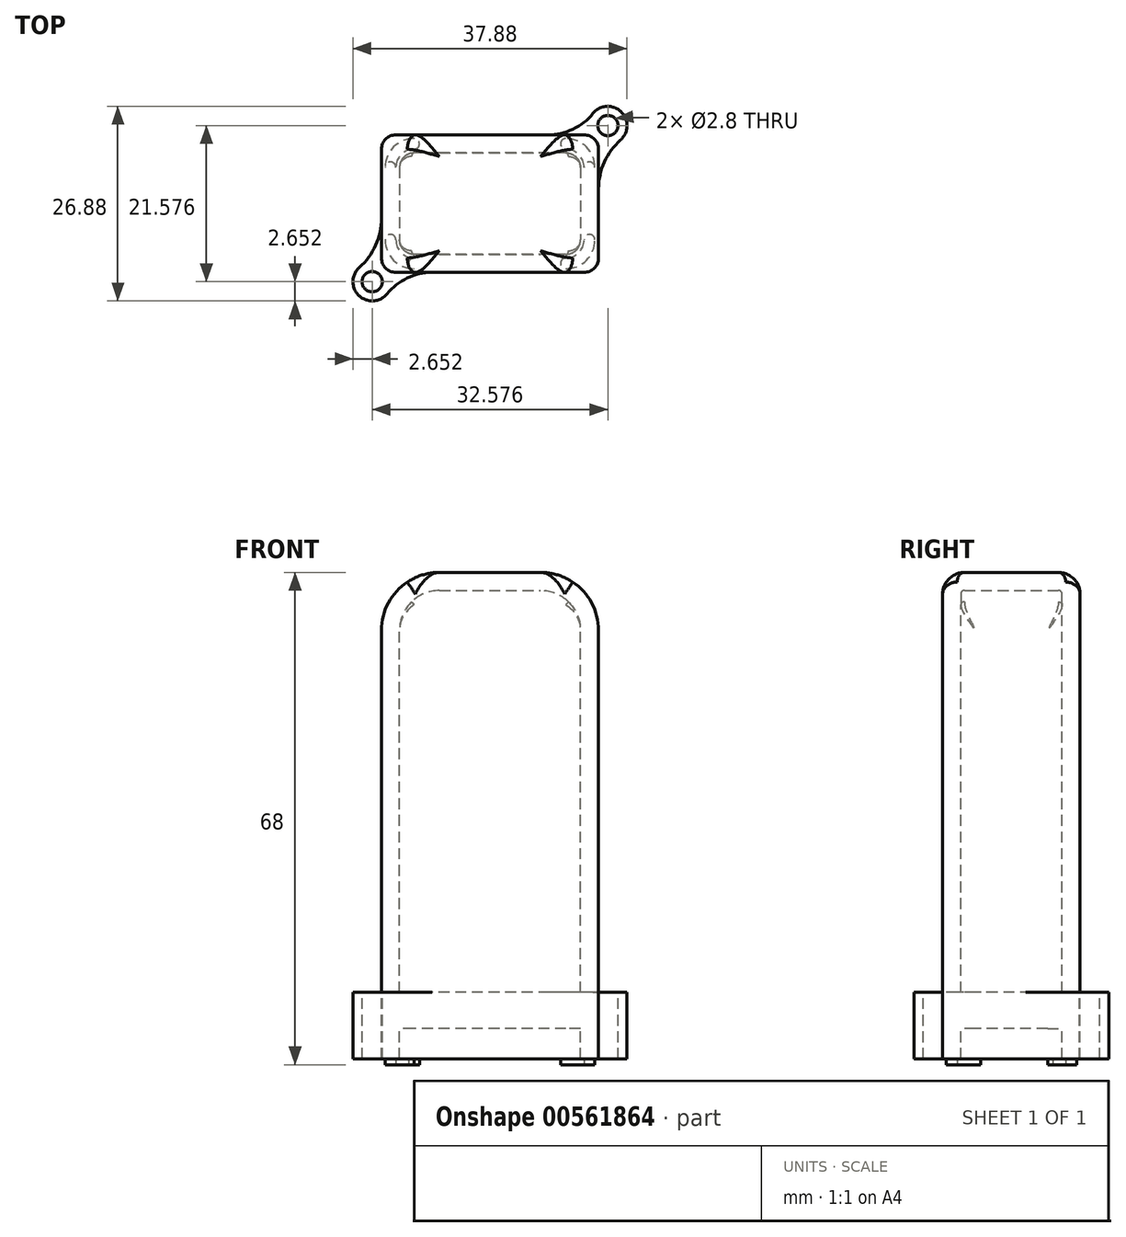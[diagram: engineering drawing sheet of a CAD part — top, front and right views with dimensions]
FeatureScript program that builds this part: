
annotation { "Feature Type Name" : "Feature", "Feature Type Description" : "" }
export const myFeature = defineFeature(function(context is Context, id is Id, definition is map)
    precondition{}
    {
        {
            var Q0;
            Q0=qCreatedBy(makeId("Top.planeOp"),FACE);
            var sketch = newSketch(context, id + "F0", { "sketchPlane" : qUnion([Q0])});
            skLineSegment(sketch, "E0.bottom", {"start": v(15, 9.5) * mm, "end": v(-15, 9.5) * mm});
            skLineSegment(sketch, "E0.top", {"start": v(15, -9.5) * mm, "end": v(-15, -9.5) * mm});
            skLineSegment(sketch, "E0.left", {"start": v(15, 9.5) * mm, "end": v(15, -9.5) * mm});
            skLineSegment(sketch, "E0.right", {"start": v(-15, 9.5) * mm, "end": v(-15, -9.5) * mm});
            skPoint(sketch, "E0.middle", {"position": v(0, 0) * mm});
            skSolve(sketch);
        }
        {
            var Q0;
            Q0 = qSketchRegion(id + "F0", true);
            extrude(context, id + "F1", {"entities" : qUnion([Q0]), "depth" : 58 * mm, "offsetDistance" : 25 * mm});
        }
        {
            var Q0;
            Q0=makeQuery(id+"F1.opExtrude","SWEPT_EDGE",EDGE,{"disambiguationData":[OSD([sQuery(id+"F0.wireOp",EDGE,"E0.top"),sQuery(id+"F0.wireOp",EDGE,"E0.right")])]});
            var Q1;
            Q1=makeQuery(id+"F1.opExtrude","SWEPT_EDGE",EDGE,{"disambiguationData":[OSD([sQuery(id+"F0.wireOp",EDGE,"E0.top"),sQuery(id+"F0.wireOp",EDGE,"E0.left")])]});
            var Q2;
            Q2=makeQuery(id+"F1.opExtrude","SWEPT_EDGE",EDGE,{"disambiguationData":[OSD([sQuery(id+"F0.wireOp",EDGE,"E0.bottom"),sQuery(id+"F0.wireOp",EDGE,"E0.left")])]});
            var Q3;
            Q3=makeQuery(id+"F1.opExtrude","SWEPT_EDGE",EDGE,{"disambiguationData":[OSD([sQuery(id+"F0.wireOp",EDGE,"E0.bottom"),sQuery(id+"F0.wireOp",EDGE,"E0.right")])]});
            fillet(context, id + "F2", {"entities" : qUnion([Q0, Q1, Q2, Q3]), "radius" : 2 * mm, "tangentPropagation" : true, "allowEdgeOverflow" : false});
        }
        {
            var Q0;
            Q0=makeQuery(id+"F1.opExtrude","CAP_EDGE",EDGE,{"disambiguationData":[OSD([sQuery(id+"F0.wireOp",EDGE,"E0.right")])],"isStart":false});
            var Q1;
            Q1=makeQuery(id+"F1.opExtrude","CAP_EDGE",EDGE,{"disambiguationData":[OSD([sQuery(id+"F0.wireOp",EDGE,"E0.left")])],"isStart":false});
            fillet(context, id + "F3", {"entities" : qUnion([Q0, Q1]), "radius" : 8 * mm, "allowEdgeOverflow" : false});
        }
        {
            var Q0;
            {var subQ0=sQuery(id+"F0.wireOp",EDGE,"E0.right");Q0=makeQuery(id+"F3.opFillet","BLEND_EDGE",EDGE,{"blendedFrom":[makeQuery(id+"F1.opExtrude","CAP_EDGE",EDGE,{"disambiguationData":[OSD([subQ0])],"isStart":false}),makeQuery(id+"F2.opFillet","BLEND_FACE",FACE,{"disambiguationData":[OSD([sQuery(id+"F0.wireOp",EDGE,"E0.top"),subQ0])]})],"blendedInto":[makeQuery(id+"F2.opFillet","BLEND_FACE",FACE,{"disambiguationData":[OSD([sQuery(id+"F0.wireOp",EDGE,"E0.top"),subQ0])]})]});}
            var Q1;
            Q1=makeQuery(id+"F3.opFillet","BLEND_EDGE",EDGE,{"blendedFrom":[makeQuery(id+"F1.opExtrude","CAP_EDGE",EDGE,{"disambiguationData":[OSD([sQuery(id+"F0.wireOp",EDGE,"E0.right")])],"isStart":false}),makeQuery(id+"F1.opExtrude","SWEPT_FACE",FACE,{"disambiguationData":[OSD([sQuery(id+"F0.wireOp",EDGE,"E0.top")])]})],"blendedInto":[makeQuery(id+"F1.opExtrude","SWEPT_FACE",FACE,{"disambiguationData":[OSD([sQuery(id+"F0.wireOp",EDGE,"E0.top")])]})]});
            var Q2;
            Q2=makeQuery(id+"F3.opFillet","BLEND_EDGE",EDGE,{"blendedFrom":[makeQuery(id+"F1.opExtrude","CAP_EDGE",EDGE,{"disambiguationData":[OSD([sQuery(id+"F0.wireOp",EDGE,"E0.right")])],"isStart":false}),makeQuery(id+"F1.opExtrude","SWEPT_FACE",FACE,{"disambiguationData":[OSD([sQuery(id+"F0.wireOp",EDGE,"E0.bottom")])]})],"blendedInto":[makeQuery(id+"F1.opExtrude","SWEPT_FACE",FACE,{"disambiguationData":[OSD([sQuery(id+"F0.wireOp",EDGE,"E0.bottom")])]})]});
            fillet(context, id + "F4", {"entities" : qUnion([Q0, Q1, Q2]), "radius" : 3 * mm, "tangentPropagation" : true, "allowEdgeOverflow" : false});
        }
        {
            var Q0;
            Q0=makeQuery(id+"F1.opExtrude","CAP_FACE",FACE,{"disambiguationData":[OSD([sQuery(id+"F0.wireOp",EDGE,"E0.bottom"),sQuery(id+"F0.wireOp",EDGE,"E0.top"),sQuery(id+"F0.wireOp",EDGE,"E0.left"),sQuery(id+"F0.wireOp",EDGE,"E0.right")])],"isStart":true});
            shell(context, id + "F5", {"entities" : qUnion([Q0]), "thickness" : 2.5 * mm});
        }
        {
            var Q0;
            {var subQ0=sQuery(id+"F0.wireOp",EDGE,"E0.top");var subQ1=sQuery(id+"F0.wireOp",EDGE,"E0.left");var subQ2=makeQuery(id+"F1.opExtrude","SWEPT_EDGE",EDGE,{"disambiguationData":[OSD([subQ0,subQ1])]});Q0=makeQuery(id+"F5.opShell","OFFSET_EDGE",EDGE,{"disambiguationData":[OSD([subQ0,subQ1]),TDD([makeQuery(id+"F2.opFillet","BLEND_EDGE",EDGE,{"blendedFrom":[subQ2,makeQuery(id+"F1.opExtrude","SWEPT_FACE",FACE,{"disambiguationData":[OSD([subQ1])]})],"blendedInto":[makeQuery(id+"F1.opExtrude","SWEPT_FACE",FACE,{"disambiguationData":[OSD([subQ1])]})]}),makeQuery(id+"F2.opFillet","BLEND_EDGE",EDGE,{"blendedFrom":[subQ2,makeQuery(id+"F1.opExtrude","SWEPT_FACE",FACE,{"disambiguationData":[OSD([subQ0])]})],"blendedInto":[makeQuery(id+"F1.opExtrude","SWEPT_FACE",FACE,{"disambiguationData":[OSD([subQ0])]})]})])]});}
            var Q1;
            {var subQ0=sQuery(id+"F0.wireOp",EDGE,"E0.bottom");var subQ1=sQuery(id+"F0.wireOp",EDGE,"E0.right");var subQ2=makeQuery(id+"F1.opExtrude","SWEPT_EDGE",EDGE,{"disambiguationData":[OSD([subQ0,subQ1])]});Q1=makeQuery(id+"F5.opShell","OFFSET_EDGE",EDGE,{"disambiguationData":[OSD([subQ0,subQ1]),TDD([makeQuery(id+"F2.opFillet","BLEND_EDGE",EDGE,{"blendedFrom":[subQ2,makeQuery(id+"F1.opExtrude","SWEPT_FACE",FACE,{"disambiguationData":[OSD([subQ1])]})],"blendedInto":[makeQuery(id+"F1.opExtrude","SWEPT_FACE",FACE,{"disambiguationData":[OSD([subQ1])]})]}),makeQuery(id+"F2.opFillet","BLEND_EDGE",EDGE,{"blendedFrom":[subQ2,makeQuery(id+"F1.opExtrude","SWEPT_FACE",FACE,{"disambiguationData":[OSD([subQ0])]})],"blendedInto":[makeQuery(id+"F1.opExtrude","SWEPT_FACE",FACE,{"disambiguationData":[OSD([subQ0])]})]})])]});}
            var Q2;
            {var subQ0=sQuery(id+"F0.wireOp",EDGE,"E0.bottom");var subQ1=sQuery(id+"F0.wireOp",EDGE,"E0.left");var subQ2=makeQuery(id+"F1.opExtrude","SWEPT_EDGE",EDGE,{"disambiguationData":[OSD([subQ0,subQ1])]});Q2=makeQuery(id+"F5.opShell","OFFSET_EDGE",EDGE,{"disambiguationData":[OSD([subQ0,subQ1]),TDD([makeQuery(id+"F2.opFillet","BLEND_EDGE",EDGE,{"blendedFrom":[subQ2,makeQuery(id+"F1.opExtrude","SWEPT_FACE",FACE,{"disambiguationData":[OSD([subQ1])]})],"blendedInto":[makeQuery(id+"F1.opExtrude","SWEPT_FACE",FACE,{"disambiguationData":[OSD([subQ1])]})]}),makeQuery(id+"F2.opFillet","BLEND_EDGE",EDGE,{"blendedFrom":[subQ2,makeQuery(id+"F1.opExtrude","SWEPT_FACE",FACE,{"disambiguationData":[OSD([subQ0])]})],"blendedInto":[makeQuery(id+"F1.opExtrude","SWEPT_FACE",FACE,{"disambiguationData":[OSD([subQ0])]})]})])]});}
            var Q3;
            {var subQ0=sQuery(id+"F0.wireOp",EDGE,"E0.top");var subQ1=sQuery(id+"F0.wireOp",EDGE,"E0.right");var subQ2=makeQuery(id+"F1.opExtrude","SWEPT_EDGE",EDGE,{"disambiguationData":[OSD([subQ0,subQ1])]});Q3=makeQuery(id+"F5.opShell","OFFSET_EDGE",EDGE,{"disambiguationData":[OSD([subQ0,subQ1]),TDD([makeQuery(id+"F2.opFillet","BLEND_EDGE",EDGE,{"blendedFrom":[subQ2,makeQuery(id+"F1.opExtrude","SWEPT_FACE",FACE,{"disambiguationData":[OSD([subQ1])]})],"blendedInto":[makeQuery(id+"F1.opExtrude","SWEPT_FACE",FACE,{"disambiguationData":[OSD([subQ1])]})]}),makeQuery(id+"F2.opFillet","BLEND_EDGE",EDGE,{"blendedFrom":[subQ2,makeQuery(id+"F1.opExtrude","SWEPT_FACE",FACE,{"disambiguationData":[OSD([subQ0])]})],"blendedInto":[makeQuery(id+"F1.opExtrude","SWEPT_FACE",FACE,{"disambiguationData":[OSD([subQ0])]})]})])]});}
            fillet(context, id + "F6", {"entities" : qUnion([Q0, Q1, Q2, Q3]), "radius" : 2 * mm, "tangentPropagation" : true, "allowEdgeOverflow" : false});
        }
        {
            var Q0;
            Q0=makeQuery(id+"F1.opExtrude","CAP_FACE",FACE,{"disambiguationData":[OSD([sQuery(id+"F0.wireOp",EDGE,"E0.bottom"),sQuery(id+"F0.wireOp",EDGE,"E0.top"),sQuery(id+"F0.wireOp",EDGE,"E0.left"),sQuery(id+"F0.wireOp",EDGE,"E0.right")])],"isStart":true});
            var sketch = newSketch(context, id + "F7", { "sketchPlane" : qUnion([Q0])});
            skLineSegment(sketch, "E1.0", {"start": v(13, -9.5) * mm, "end": v(-13, -9.5) * mm});
            skArc(sketch, "E1.1", {"start": v(-15, -7.5) * mm, "mid": v(-14.41, -8.91) * mm, "end": v(-13, -9.5) * mm});
            skLineSegment(sketch, "E1.2", {"start": v(-15, -7.5) * mm, "end": v(-15, 7.5) * mm});
            skLineSegment(sketch, "E1.3", {"start": v(15, -7.5) * mm, "end": v(15, 7.5) * mm});
            skArc(sketch, "E1.4", {"start": v(15, 7.5) * mm, "mid": v(14.41, 8.91) * mm, "end": v(13, 9.5) * mm});
            skLineSegment(sketch, "E1.5", {"start": v(13, 9.5) * mm, "end": v(-13, 9.5) * mm});
            skArc(sketch, "E1.6", {"start": v(-13, 9.5) * mm, "mid": v(-14.41, 8.91) * mm, "end": v(-15, 7.5) * mm});
            skArc(sketch, "E2", {"start": v(13, -9.5) * mm, "mid": v(14.41, -8.91) * mm, "end": v(15, -7.5) * mm});
            skCircle(sketch, "E3", {"center": v(-16.29, 10.79) * mm, "radius": 2.65 * mm});
            skLineSegment(sketch, "E4", {"start": v(-13, 7.5) * mm, "end": v(-16.29, 10.79) * mm});
            skLineSegment(sketch, "E5", {"start": v(-13, 7.5) * mm, "end": v(-19.8, 7.5) * mm});
            skCircle(sketch, "E6", {"center": v(-16.29, 10.79) * mm, "radius": 1.4 * mm});
            skArc(sketch, "E7", {"start": v(-14.23, 12.46) * mm, "mid": v(-11.45, 10.28) * mm, "end": v(-8, 9.5) * mm});
            skArc(sketch, "E8", {"start": v(-15, 2) * mm, "mid": v(-15.8, 5.73) * mm, "end": v(-18.05, 8.81) * mm});
            skCircle(sketch, "E9.1.0", {"center": v(16.29, -10.79) * mm, "radius": 2.65 * mm});
            skCircle(sketch, "E9.1.1", {"center": v(16.29, -10.79) * mm, "radius": 1.4 * mm});
            skArc(sketch, "E9.1.2", {"start": v(14.23, -12.46) * mm, "mid": v(11.45, -10.28) * mm, "end": v(8, -9.5) * mm});
            skArc(sketch, "E9.1.3", {"start": v(15, -2) * mm, "mid": v(15.8, -5.73) * mm, "end": v(18.05, -8.81) * mm});
            skPoint(sketch, "E9.center", {"position": v(0, 0) * mm});
            skSolve(sketch);
        }
        {
            var Q0;
            {var subQ3=sQuery(id+"F7.wireOp",EDGE,"E9.1.2");Q0=makeQuery(id+"F7.imprint","IMPRINT",FACE,{"disambiguationData":[TD([[makeQuery(id+"F7.imprint","IMPRINT",EDGE,{"derivedFrom":subQ3}),-1.0]])]});}
            var Q1;
            {var subQ1=sQuery(id+"F7.wireOp",EDGE,"E1.2");var subQ3=sQuery(id+"F7.wireOp",EDGE,"E8");var subQ4=makeQuery(id+"F7.imprint","INTERSECT",VERTEX,{"derivedFrom":[subQ1,subQ3]});Q1=makeQuery(id+"F7.imprint","IMPRINT",FACE,{"disambiguationData":[TD([[makeQuery(id+"F7.imprint","IMPRINT",EDGE,{"disambiguationData":[TD([[subQ4,-1.0]])],"derivedFrom":subQ3}),-1.0]])]});}
            var Q2;
            {var subQ3=sQuery(id+"F7.wireOp",EDGE,"E9.1.3");Q2=makeQuery(id+"F7.imprint","IMPRINT",FACE,{"disambiguationData":[TD([[makeQuery(id+"F7.imprint","IMPRINT",EDGE,{"derivedFrom":subQ3}),-1.0]])]});}
            var Q3;
            {var subQ3=sQuery(id+"F7.wireOp",EDGE,"E7");Q3=makeQuery(id+"F7.imprint","IMPRINT",FACE,{"disambiguationData":[TD([[makeQuery(id+"F7.imprint","IMPRINT",EDGE,{"derivedFrom":subQ3}),-1.0]])]});}
            var Q4;
            {var subQ3=sQuery(id+"F7.wireOp",EDGE,"E3");var subQ5=sQuery(id+"F7.wireOp",EDGE,"E8");var subQ6=makeQuery(id+"F7.imprint","INTERSECT",VERTEX,{"derivedFrom":[subQ3,subQ5]});Q4=makeQuery(id+"F7.imprint","IMPRINT",FACE,{"disambiguationData":[TD([[makeQuery(id+"F7.imprint","IMPRINT",EDGE,{"disambiguationData":[TD([[subQ6,1.0]])],"derivedFrom":subQ5}),-1.0]])]});}
            var Q5;
            Q5=makeQuery(id+"F7.imprint","IMPRINT",FACE,{"disambiguationData":[TD([[makeQuery(id+"F7.imprint","IMPRINT",EDGE,{"derivedFrom":sQuery(id+"F7.wireOp",EDGE,"E6")}),-1.0]])]});
            var Q6;
            Q6=makeQuery(id+"F7.imprint","IMPRINT",FACE,{"disambiguationData":[TD([[makeQuery(id+"F7.imprint","IMPRINT",EDGE,{"derivedFrom":sQuery(id+"F7.wireOp",EDGE,"E9.1.1")}),-1.0]])]});
            var Q7;
            {var subQ27=sQuery(id+"F7.wireOp",EDGE,"E1.1");Q7=makeQuery(id+"F7.imprint","IMPRINT",FACE,{"disambiguationData":[TD([[makeQuery(id+"F7.imprint","IMPRINT",EDGE,{"derivedFrom":subQ27}),1.0]])]});}
            var Q8;
            {var subQ0=sQuery(id+"F7.wireOp",EDGE,"E5");var subQ3=sQuery(id+"F7.wireOp",EDGE,"E4");var subQ5=makeQuery(id+"F7.imprint","INTERSECT",VERTEX,{"derivedFrom":[subQ3,subQ0]});Q8=makeQuery(id+"F7.imprint","IMPRINT",FACE,{"disambiguationData":[TD([[makeQuery(id+"F7.imprint","IMPRINT",EDGE,{"disambiguationData":[TD([[subQ5,-1.0]])],"derivedFrom":subQ3}),1.0]])]});}
            extrude(context, id + "F8", {"entities" : qUnion([Q0, Q1, Q2, Q3, Q4, Q5, Q6, Q7, Q8]), "depth" : 5 * mm, "offsetDistance" : 25 * mm});
        }
        {
            var Q0;
            Q0=makeQuery(id+"F8.opExtrude","CAP_FACE",FACE,{"disambiguationData":[OSD([sQuery(id+"F0.wireOp",EDGE,"E0.bottom"),sQuery(id+"F0.wireOp",EDGE,"E0.top"),sQuery(id+"F0.wireOp",EDGE,"E0.left"),sQuery(id+"F0.wireOp",EDGE,"E0.right"),sQuery(id+"F7.wireOp",EDGE,"E1.0"),sQuery(id+"F7.wireOp",EDGE,"E1.1"),sQuery(id+"F7.wireOp",EDGE,"E1.2"),sQuery(id+"F7.wireOp",EDGE,"E1.3"),sQuery(id+"F7.wireOp",EDGE,"E1.4"),sQuery(id+"F7.wireOp",EDGE,"E1.5"),sQuery(id+"F7.wireOp",EDGE,"E3"),sQuery(id+"F7.wireOp",EDGE,"E6"),sQuery(id+"F7.wireOp",EDGE,"E7"),sQuery(id+"F7.wireOp",EDGE,"E8"),sQuery(id+"F7.wireOp",EDGE,"E9.1.0"),sQuery(id+"F7.wireOp",EDGE,"E9.1.1"),sQuery(id+"F7.wireOp",EDGE,"E9.1.2"),sQuery(id+"F7.wireOp",EDGE,"E9.1.3")])],"isStart":false});
            extrude(context, id + "F9", {"entities" : qUnion([Q0]), "depth" : 5 * mm, "offsetDistance" : 25 * mm});
        }
        {
            var Q0;
            Q0=makeQuery(id+"F9.opExtrude","CAP_FACE",FACE,{"disambiguationData":[OSD([sQuery(id+"F0.wireOp",EDGE,"E0.bottom"),sQuery(id+"F0.wireOp",EDGE,"E0.top"),sQuery(id+"F0.wireOp",EDGE,"E0.left"),sQuery(id+"F0.wireOp",EDGE,"E0.right"),sQuery(id+"F7.wireOp",EDGE,"E1.0"),sQuery(id+"F7.wireOp",EDGE,"E1.1"),sQuery(id+"F7.wireOp",EDGE,"E1.2"),sQuery(id+"F7.wireOp",EDGE,"E1.3"),sQuery(id+"F7.wireOp",EDGE,"E1.4"),sQuery(id+"F7.wireOp",EDGE,"E1.5"),sQuery(id+"F7.wireOp",EDGE,"E3"),sQuery(id+"F7.wireOp",EDGE,"E6"),sQuery(id+"F7.wireOp",EDGE,"E7"),sQuery(id+"F7.wireOp",EDGE,"E8"),sQuery(id+"F7.wireOp",EDGE,"E9.1.0"),sQuery(id+"F7.wireOp",EDGE,"E9.1.1"),sQuery(id+"F7.wireOp",EDGE,"E9.1.2"),sQuery(id+"F7.wireOp",EDGE,"E9.1.3")])],"isStart":false});
            var sketch = newSketch(context, id + "F10", { "sketchPlane" : qUnion([Q0])});
            skArc(sketch, "E10.0", {"start": v(10.5, 8.25) * mm, "mid": v(12.8, 7.3) * mm, "end": v(13.75, 5) * mm});
            skLineSegment(sketch, "E10.1", {"start": v(13.75, -5) * mm, "end": v(13.75, 5) * mm});
            skLineSegment(sketch, "E10.2", {"start": v(10.5, 8.25) * mm, "end": v(-10.5, 8.25) * mm});
            skArc(sketch, "E10.3", {"start": v(13.75, -5) * mm, "mid": v(12.8, -7.3) * mm, "end": v(10.5, -8.25) * mm});
            skArc(sketch, "E10.4", {"start": v(-13.75, 5) * mm, "mid": v(-12.8, 7.3) * mm, "end": v(-10.5, 8.25) * mm});
            skLineSegment(sketch, "E10.5", {"start": v(-13.75, -5) * mm, "end": v(-13.75, 5) * mm});
            skArc(sketch, "E10.6", {"start": v(-10.5, -8.25) * mm, "mid": v(-12.8, -7.3) * mm, "end": v(-13.75, -5) * mm});
            skLineSegment(sketch, "E10.7", {"start": v(10.5, -8.25) * mm, "end": v(-10.5, -8.25) * mm});
            skArc(sketch, "E11.0.startCap", {"start": v(10.5, 9) * mm, "mid": v(11.25, 8.25) * mm, "end": v(10.5, 7.5) * mm});
            skArc(sketch, "E11.0.endCap", {"start": v(-10.5, 7.5) * mm, "mid": v(-11.25, 8.25) * mm, "end": v(-10.5, 9) * mm});
            skLineSegment(sketch, "E11.0.left", {"start": v(10.5, 7.5) * mm, "end": v(-10.5, 7.5) * mm});
            skLineSegment(sketch, "E11.0.right", {"start": v(10.5, 9) * mm, "end": v(-10.5, 9) * mm});
            skArc(sketch, "E11.1.startCap", {"start": v(-13, 5) * mm, "mid": v(-13.75, 4.25) * mm, "end": v(-14.5, 5) * mm});
            skArc(sketch, "E11.1.endCap", {"start": v(-10.5, 9) * mm, "mid": v(-9.75, 8.25) * mm, "end": v(-10.5, 7.5) * mm});
            skArc(sketch, "E11.1.left", {"start": v(-14.5, 5) * mm, "mid": v(-13.33, 7.83) * mm, "end": v(-10.5, 9) * mm});
            skArc(sketch, "E11.1.right", {"start": v(-13, 5) * mm, "mid": v(-12.27, 6.77) * mm, "end": v(-10.5, 7.5) * mm});
            skArc(sketch, "E11.2.startCap", {"start": v(-13, -5) * mm, "mid": v(-13.75, -5.75) * mm, "end": v(-14.5, -5) * mm});
            skArc(sketch, "E11.2.endCap", {"start": v(-14.5, 5) * mm, "mid": v(-13.75, 5.75) * mm, "end": v(-13, 5) * mm});
            skLineSegment(sketch, "E11.2.left", {"start": v(-14.5, -5) * mm, "end": v(-14.5, 5) * mm});
            skLineSegment(sketch, "E11.2.right", {"start": v(-13, -5) * mm, "end": v(-13, 5) * mm});
            skArc(sketch, "E11.3.startCap", {"start": v(-10.5, -7.5) * mm, "mid": v(-9.75, -8.25) * mm, "end": v(-10.5, -9) * mm});
            skArc(sketch, "E11.3.endCap", {"start": v(-14.5, -5) * mm, "mid": v(-13.75, -4.25) * mm, "end": v(-13, -5) * mm});
            skArc(sketch, "E11.3.left", {"start": v(-10.5, -9) * mm, "mid": v(-13.33, -7.83) * mm, "end": v(-14.5, -5) * mm});
            skArc(sketch, "E11.3.right", {"start": v(-10.5, -7.5) * mm, "mid": v(-12.27, -6.77) * mm, "end": v(-13, -5) * mm});
            skArc(sketch, "E11.4.startCap", {"start": v(10.5, -7.5) * mm, "mid": v(11.25, -8.25) * mm, "end": v(10.5, -9) * mm});
            skArc(sketch, "E11.4.endCap", {"start": v(-10.5, -9) * mm, "mid": v(-11.25, -8.25) * mm, "end": v(-10.5, -7.5) * mm});
            skLineSegment(sketch, "E11.4.left", {"start": v(10.5, -9) * mm, "end": v(-10.5, -9) * mm});
            skLineSegment(sketch, "E11.4.right", {"start": v(10.5, -7.5) * mm, "end": v(-10.5, -7.5) * mm});
            skArc(sketch, "E11.5.startCap", {"start": v(13, -5) * mm, "mid": v(13.75, -4.25) * mm, "end": v(14.5, -5) * mm});
            skArc(sketch, "E11.5.endCap", {"start": v(10.5, -9) * mm, "mid": v(9.75, -8.25) * mm, "end": v(10.5, -7.5) * mm});
            skArc(sketch, "E11.5.left", {"start": v(14.5, -5) * mm, "mid": v(13.33, -7.83) * mm, "end": v(10.5, -9) * mm});
            skArc(sketch, "E11.5.right", {"start": v(13, -5) * mm, "mid": v(12.27, -6.77) * mm, "end": v(10.5, -7.5) * mm});
            skArc(sketch, "E11.6.startCap", {"start": v(14.5, -5) * mm, "mid": v(13.75, -5.75) * mm, "end": v(13, -5) * mm});
            skArc(sketch, "E11.6.endCap", {"start": v(13, 5) * mm, "mid": v(13.75, 5.75) * mm, "end": v(14.5, 5) * mm});
            skLineSegment(sketch, "E11.6.left", {"start": v(13, -5) * mm, "end": v(13, 5) * mm});
            skLineSegment(sketch, "E11.6.right", {"start": v(14.5, -5) * mm, "end": v(14.5, 5) * mm});
            skArc(sketch, "E11.7.startCap", {"start": v(10.5, 7.5) * mm, "mid": v(9.75, 8.25) * mm, "end": v(10.5, 9) * mm});
            skArc(sketch, "E11.7.endCap", {"start": v(14.5, 5) * mm, "mid": v(13.75, 4.25) * mm, "end": v(13, 5) * mm});
            skArc(sketch, "E11.7.left", {"start": v(10.5, 9) * mm, "mid": v(13.33, 7.83) * mm, "end": v(14.5, 5) * mm});
            skArc(sketch, "E11.7.right", {"start": v(10.5, 7.5) * mm, "mid": v(12.27, 6.77) * mm, "end": v(13, 5) * mm});
            skSolve(sketch);
        }
        {
            var Q0;
            {var subQ0=sQuery(id+"F10.wireOp",EDGE,"E10.2");var subQ1=sQuery(id+"F10.wireOp",EDGE,"E10.0");var subQ2=makeQuery(id+"F10.imprint","INTERSECT",VERTEX,{"derivedFrom":[subQ1,subQ0]});Q0=makeQuery(id+"F10.imprint","IMPRINT",FACE,{"disambiguationData":[TD([[makeQuery(id+"F10.imprint","IMPRINT",EDGE,{"disambiguationData":[TD([[subQ2,-1.0]])],"derivedFrom":subQ1}),1.0]])]});}
            var Q1;
            {var subQ0=sQuery(id+"F10.wireOp",EDGE,"E10.1");var subQ1=sQuery(id+"F10.wireOp",EDGE,"E10.0");var subQ2=makeQuery(id+"F10.imprint","INTERSECT",VERTEX,{"derivedFrom":[subQ1,subQ0]});Q1=makeQuery(id+"F10.imprint","IMPRINT",FACE,{"disambiguationData":[TD([[makeQuery(id+"F10.imprint","IMPRINT",EDGE,{"disambiguationData":[TD([[subQ2,1.0]])],"derivedFrom":subQ1}),1.0]])]});}
            var Q2;
            {var subQ0=sQuery(id+"F10.wireOp",EDGE,"E10.3");var subQ1=sQuery(id+"F10.wireOp",EDGE,"E10.1");var subQ2=makeQuery(id+"F10.imprint","INTERSECT",VERTEX,{"derivedFrom":[subQ1,subQ0]});Q2=makeQuery(id+"F10.imprint","IMPRINT",FACE,{"disambiguationData":[TD([[makeQuery(id+"F10.imprint","IMPRINT",EDGE,{"disambiguationData":[TD([[subQ2,-1.0]])],"derivedFrom":subQ1}),-1.0]])]});}
            var Q3;
            {var subQ0=sQuery(id+"F10.wireOp",EDGE,"E10.4");var subQ1=sQuery(id+"F10.wireOp",EDGE,"E10.2");var subQ2=makeQuery(id+"F10.imprint","INTERSECT",VERTEX,{"derivedFrom":[subQ1,subQ0]});Q3=makeQuery(id+"F10.imprint","IMPRINT",FACE,{"disambiguationData":[TD([[makeQuery(id+"F10.imprint","IMPRINT",EDGE,{"disambiguationData":[TD([[subQ2,1.0]])],"derivedFrom":subQ1}),-1.0]])]});}
            var Q4;
            {var subQ0=sQuery(id+"F10.wireOp",EDGE,"E10.7");var subQ1=sQuery(id+"F10.wireOp",EDGE,"E10.3");var subQ2=makeQuery(id+"F10.imprint","INTERSECT",VERTEX,{"derivedFrom":[subQ1,subQ0]});Q4=makeQuery(id+"F10.imprint","IMPRINT",FACE,{"disambiguationData":[TD([[makeQuery(id+"F10.imprint","IMPRINT",EDGE,{"disambiguationData":[TD([[subQ2,1.0]])],"derivedFrom":subQ1}),1.0]])]});}
            var Q5;
            {var subQ0=sQuery(id+"F10.wireOp",EDGE,"E10.5");var subQ1=sQuery(id+"F10.wireOp",EDGE,"E10.4");var subQ2=makeQuery(id+"F10.imprint","INTERSECT",VERTEX,{"derivedFrom":[subQ1,subQ0]});Q5=makeQuery(id+"F10.imprint","IMPRINT",FACE,{"disambiguationData":[TD([[makeQuery(id+"F10.imprint","IMPRINT",EDGE,{"disambiguationData":[TD([[subQ2,-1.0]])],"derivedFrom":subQ1}),1.0]])]});}
            var Q6;
            {var subQ0=sQuery(id+"F10.wireOp",EDGE,"E10.7");var subQ1=sQuery(id+"F10.wireOp",EDGE,"E10.6");var subQ2=makeQuery(id+"F10.imprint","INTERSECT",VERTEX,{"derivedFrom":[subQ1,subQ0]});Q6=makeQuery(id+"F10.imprint","IMPRINT",FACE,{"disambiguationData":[TD([[makeQuery(id+"F10.imprint","IMPRINT",EDGE,{"disambiguationData":[TD([[subQ2,-1.0]])],"derivedFrom":subQ1}),1.0]])]});}
            var Q7;
            {var subQ5=sQuery(id+"F10.wireOp",EDGE,"E11.7.left");Q7=makeQuery(id+"F10.imprint","IMPRINT",FACE,{"disambiguationData":[TD([[makeQuery(id+"F10.imprint","IMPRINT",EDGE,{"derivedFrom":subQ5}),-1.0]])]});}
            var Q8;
            {var subQ5=sQuery(id+"F10.wireOp",EDGE,"E11.6.right");Q8=makeQuery(id+"F10.imprint","IMPRINT",FACE,{"disambiguationData":[TD([[makeQuery(id+"F10.imprint","IMPRINT",EDGE,{"derivedFrom":subQ5}),1.0]])]});}
            var Q9;
            {var subQ5=sQuery(id+"F10.wireOp",EDGE,"E11.0.right");Q9=makeQuery(id+"F10.imprint","IMPRINT",FACE,{"disambiguationData":[TD([[makeQuery(id+"F10.imprint","IMPRINT",EDGE,{"derivedFrom":subQ5}),1.0]])]});}
            var Q10;
            {var subQ5=sQuery(id+"F10.wireOp",EDGE,"E11.5.left");Q10=makeQuery(id+"F10.imprint","IMPRINT",FACE,{"disambiguationData":[TD([[makeQuery(id+"F10.imprint","IMPRINT",EDGE,{"derivedFrom":subQ5}),-1.0]])]});}
            var Q11;
            {var subQ5=sQuery(id+"F10.wireOp",EDGE,"E11.1.left");Q11=makeQuery(id+"F10.imprint","IMPRINT",FACE,{"disambiguationData":[TD([[makeQuery(id+"F10.imprint","IMPRINT",EDGE,{"derivedFrom":subQ5}),-1.0]])]});}
            var Q12;
            {var subQ5=sQuery(id+"F10.wireOp",EDGE,"E11.2.left");Q12=makeQuery(id+"F10.imprint","IMPRINT",FACE,{"disambiguationData":[TD([[makeQuery(id+"F10.imprint","IMPRINT",EDGE,{"derivedFrom":subQ5}),-1.0]])]});}
            var Q13;
            {var subQ5=sQuery(id+"F10.wireOp",EDGE,"E11.3.left");Q13=makeQuery(id+"F10.imprint","IMPRINT",FACE,{"disambiguationData":[TD([[makeQuery(id+"F10.imprint","IMPRINT",EDGE,{"derivedFrom":subQ5}),-1.0]])]});}
            var Q14;
            {var subQ5=sQuery(id+"F10.wireOp",EDGE,"E11.4.left");Q14=makeQuery(id+"F10.imprint","IMPRINT",FACE,{"disambiguationData":[TD([[makeQuery(id+"F10.imprint","IMPRINT",EDGE,{"derivedFrom":subQ5}),-1.0]])]});}
            var Q15;
            {var subQ5=sQuery(id+"F10.wireOp",EDGE,"E11.7.right");Q15=makeQuery(id+"F10.imprint","IMPRINT",FACE,{"disambiguationData":[TD([[makeQuery(id+"F10.imprint","IMPRINT",EDGE,{"derivedFrom":subQ5}),1.0]])]});}
            var Q16;
            {var subQ0=sQuery(id+"F10.wireOp",EDGE,"E10.2");var subQ1=sQuery(id+"F10.wireOp",EDGE,"E10.0");var subQ2=makeQuery(id+"F10.imprint","INTERSECT",VERTEX,{"derivedFrom":[subQ1,subQ0]});Q16=makeQuery(id+"F10.imprint","IMPRINT",FACE,{"disambiguationData":[TD([[makeQuery(id+"F10.imprint","IMPRINT",EDGE,{"disambiguationData":[TD([[subQ2,-1.0]])],"derivedFrom":subQ1}),-1.0]])]});}
            var Q17;
            {var subQ5=sQuery(id+"F10.wireOp",EDGE,"E11.0.left");Q17=makeQuery(id+"F10.imprint","IMPRINT",FACE,{"disambiguationData":[TD([[makeQuery(id+"F10.imprint","IMPRINT",EDGE,{"derivedFrom":subQ5}),-1.0]])]});}
            var Q18;
            {var subQ0=sQuery(id+"F10.wireOp",EDGE,"E10.4");var subQ1=sQuery(id+"F10.wireOp",EDGE,"E10.2");var subQ2=makeQuery(id+"F10.imprint","INTERSECT",VERTEX,{"derivedFrom":[subQ1,subQ0]});Q18=makeQuery(id+"F10.imprint","IMPRINT",FACE,{"disambiguationData":[TD([[makeQuery(id+"F10.imprint","IMPRINT",EDGE,{"disambiguationData":[TD([[subQ2,1.0]])],"derivedFrom":subQ1}),1.0]])]});}
            var Q19;
            {var subQ5=sQuery(id+"F10.wireOp",EDGE,"E11.1.right");Q19=makeQuery(id+"F10.imprint","IMPRINT",FACE,{"disambiguationData":[TD([[makeQuery(id+"F10.imprint","IMPRINT",EDGE,{"derivedFrom":subQ5}),1.0]])]});}
            var Q20;
            {var subQ0=sQuery(id+"F10.wireOp",EDGE,"E10.5");var subQ1=sQuery(id+"F10.wireOp",EDGE,"E10.4");var subQ2=makeQuery(id+"F10.imprint","INTERSECT",VERTEX,{"derivedFrom":[subQ1,subQ0]});Q20=makeQuery(id+"F10.imprint","IMPRINT",FACE,{"disambiguationData":[TD([[makeQuery(id+"F10.imprint","IMPRINT",EDGE,{"disambiguationData":[TD([[subQ2,-1.0]])],"derivedFrom":subQ1}),-1.0]])]});}
            var Q21;
            {var subQ5=sQuery(id+"F10.wireOp",EDGE,"E11.2.right");Q21=makeQuery(id+"F10.imprint","IMPRINT",FACE,{"disambiguationData":[TD([[makeQuery(id+"F10.imprint","IMPRINT",EDGE,{"derivedFrom":subQ5}),1.0]])]});}
            var Q22;
            {var subQ0=sQuery(id+"F10.wireOp",EDGE,"E10.6");var subQ1=sQuery(id+"F10.wireOp",EDGE,"E10.5");var subQ2=makeQuery(id+"F10.imprint","INTERSECT",VERTEX,{"derivedFrom":[subQ1,subQ0]});Q22=makeQuery(id+"F10.imprint","IMPRINT",FACE,{"disambiguationData":[TD([[makeQuery(id+"F10.imprint","IMPRINT",EDGE,{"disambiguationData":[TD([[subQ2,-1.0]])],"derivedFrom":subQ1}),-1.0]])]});}
            var Q23;
            {var subQ5=sQuery(id+"F10.wireOp",EDGE,"E11.3.right");Q23=makeQuery(id+"F10.imprint","IMPRINT",FACE,{"disambiguationData":[TD([[makeQuery(id+"F10.imprint","IMPRINT",EDGE,{"derivedFrom":subQ5}),1.0]])]});}
            var Q24;
            {var subQ0=sQuery(id+"F10.wireOp",EDGE,"E10.6");var subQ1=sQuery(id+"F10.wireOp",EDGE,"E10.5");var subQ2=makeQuery(id+"F10.imprint","INTERSECT",VERTEX,{"derivedFrom":[subQ1,subQ0]});Q24=makeQuery(id+"F10.imprint","IMPRINT",FACE,{"disambiguationData":[TD([[makeQuery(id+"F10.imprint","IMPRINT",EDGE,{"disambiguationData":[TD([[subQ2,-1.0]])],"derivedFrom":subQ1}),1.0]])]});}
            var Q25;
            {var subQ0=sQuery(id+"F10.wireOp",EDGE,"E10.7");var subQ1=sQuery(id+"F10.wireOp",EDGE,"E10.6");var subQ2=makeQuery(id+"F10.imprint","INTERSECT",VERTEX,{"derivedFrom":[subQ1,subQ0]});Q25=makeQuery(id+"F10.imprint","IMPRINT",FACE,{"disambiguationData":[TD([[makeQuery(id+"F10.imprint","IMPRINT",EDGE,{"disambiguationData":[TD([[subQ2,-1.0]])],"derivedFrom":subQ1}),-1.0]])]});}
            var Q26;
            {var subQ5=sQuery(id+"F10.wireOp",EDGE,"E11.4.right");Q26=makeQuery(id+"F10.imprint","IMPRINT",FACE,{"disambiguationData":[TD([[makeQuery(id+"F10.imprint","IMPRINT",EDGE,{"derivedFrom":subQ5}),1.0]])]});}
            var Q27;
            {var subQ0=sQuery(id+"F10.wireOp",EDGE,"E10.7");var subQ1=sQuery(id+"F10.wireOp",EDGE,"E10.3");var subQ2=makeQuery(id+"F10.imprint","INTERSECT",VERTEX,{"derivedFrom":[subQ1,subQ0]});Q27=makeQuery(id+"F10.imprint","IMPRINT",FACE,{"disambiguationData":[TD([[makeQuery(id+"F10.imprint","IMPRINT",EDGE,{"disambiguationData":[TD([[subQ2,1.0]])],"derivedFrom":subQ1}),-1.0]])]});}
            var Q28;
            {var subQ5=sQuery(id+"F10.wireOp",EDGE,"E11.5.right");Q28=makeQuery(id+"F10.imprint","IMPRINT",FACE,{"disambiguationData":[TD([[makeQuery(id+"F10.imprint","IMPRINT",EDGE,{"derivedFrom":subQ5}),1.0]])]});}
            var Q29;
            {var subQ0=sQuery(id+"F10.wireOp",EDGE,"E10.3");var subQ1=sQuery(id+"F10.wireOp",EDGE,"E10.1");var subQ2=makeQuery(id+"F10.imprint","INTERSECT",VERTEX,{"derivedFrom":[subQ1,subQ0]});Q29=makeQuery(id+"F10.imprint","IMPRINT",FACE,{"disambiguationData":[TD([[makeQuery(id+"F10.imprint","IMPRINT",EDGE,{"disambiguationData":[TD([[subQ2,-1.0]])],"derivedFrom":subQ1}),1.0]])]});}
            var Q30;
            {var subQ5=sQuery(id+"F10.wireOp",EDGE,"E11.6.left");Q30=makeQuery(id+"F10.imprint","IMPRINT",FACE,{"disambiguationData":[TD([[makeQuery(id+"F10.imprint","IMPRINT",EDGE,{"derivedFrom":subQ5}),-1.0]])]});}
            var Q31;
            {var subQ0=sQuery(id+"F10.wireOp",EDGE,"E10.1");var subQ1=sQuery(id+"F10.wireOp",EDGE,"E10.0");var subQ2=makeQuery(id+"F10.imprint","INTERSECT",VERTEX,{"derivedFrom":[subQ1,subQ0]});Q31=makeQuery(id+"F10.imprint","IMPRINT",FACE,{"disambiguationData":[TD([[makeQuery(id+"F10.imprint","IMPRINT",EDGE,{"disambiguationData":[TD([[subQ2,1.0]])],"derivedFrom":subQ1}),-1.0]])]});}
            extrude(context, id + "F11", {"entities" : qUnion([Q0, Q1, Q2, Q3, Q4, Q5, Q6, Q7, Q8, Q9, Q10, Q11, Q12, Q13, Q14, Q15, Q16, Q17, Q18, Q19, Q20, Q21, Q22, Q23, Q24, Q25, Q26, Q27, Q28, Q29, Q30, Q31]), "operationType" : NewBodyOperationType.REMOVE, "oppositeDirection" : true, "depth" : .8 * mm, "offsetDistance" : 25 * mm});
        }
        {
            var Q0;
            Q0=makeQuery(id+"F8.opExtrude","CAP_FACE",FACE,{"disambiguationData":[OSD([sQuery(id+"F0.wireOp",EDGE,"E0.bottom"),sQuery(id+"F0.wireOp",EDGE,"E0.top"),sQuery(id+"F0.wireOp",EDGE,"E0.left"),sQuery(id+"F0.wireOp",EDGE,"E0.right"),sQuery(id+"F7.wireOp",EDGE,"E1.0"),sQuery(id+"F7.wireOp",EDGE,"E1.1"),sQuery(id+"F7.wireOp",EDGE,"E1.2"),sQuery(id+"F7.wireOp",EDGE,"E1.3"),sQuery(id+"F7.wireOp",EDGE,"E1.4"),sQuery(id+"F7.wireOp",EDGE,"E1.5"),sQuery(id+"F7.wireOp",EDGE,"E3"),sQuery(id+"F7.wireOp",EDGE,"E6"),sQuery(id+"F7.wireOp",EDGE,"E7"),sQuery(id+"F7.wireOp",EDGE,"E8"),sQuery(id+"F7.wireOp",EDGE,"E9.1.0"),sQuery(id+"F7.wireOp",EDGE,"E9.1.1"),sQuery(id+"F7.wireOp",EDGE,"E9.1.2"),sQuery(id+"F7.wireOp",EDGE,"E9.1.3")])],"isStart":true});
            var sketch = newSketch(context, id + "F12", { "sketchPlane" : qUnion([Q0])});
            skArc(sketch, "E12.0", {"start": v(-10.5, 7) * mm, "mid": v(-11.91, 6.41) * mm, "end": v(-12.5, 5) * mm});
            skLineSegment(sketch, "E12.1", {"start": v(10.5, 7) * mm, "end": v(-10.5, 7) * mm});
            skLineSegment(sketch, "E12.2", {"start": v(-12.5, 5) * mm, "end": v(-12.5, -5) * mm});
            skArc(sketch, "E12.3", {"start": v(12.5, 5) * mm, "mid": v(11.91, 6.41) * mm, "end": v(10.5, 7) * mm});
            skArc(sketch, "E12.4", {"start": v(-12.5, -5) * mm, "mid": v(-11.91, -6.41) * mm, "end": v(-10.5, -7) * mm});
            skLineSegment(sketch, "E12.5", {"start": v(10.5, -7) * mm, "end": v(-10.5, -7) * mm});
            skArc(sketch, "E12.6", {"start": v(10.5, -7) * mm, "mid": v(11.91, -6.41) * mm, "end": v(12.5, -5) * mm});
            skLineSegment(sketch, "E12.7", {"start": v(12.5, 5) * mm, "end": v(12.5, -5) * mm});
            skSolve(sketch);
        }
        {
            var Q0;
            Q0 = qSketchRegion(id + "F12", true);
            extrude(context, id + "F13", {"entities" : qUnion([Q0]), "operationType" : NewBodyOperationType.ADD, "oppositeDirection" : true, "depth" : 5 * mm, "offsetDistance" : 25 * mm});
        }
    });
